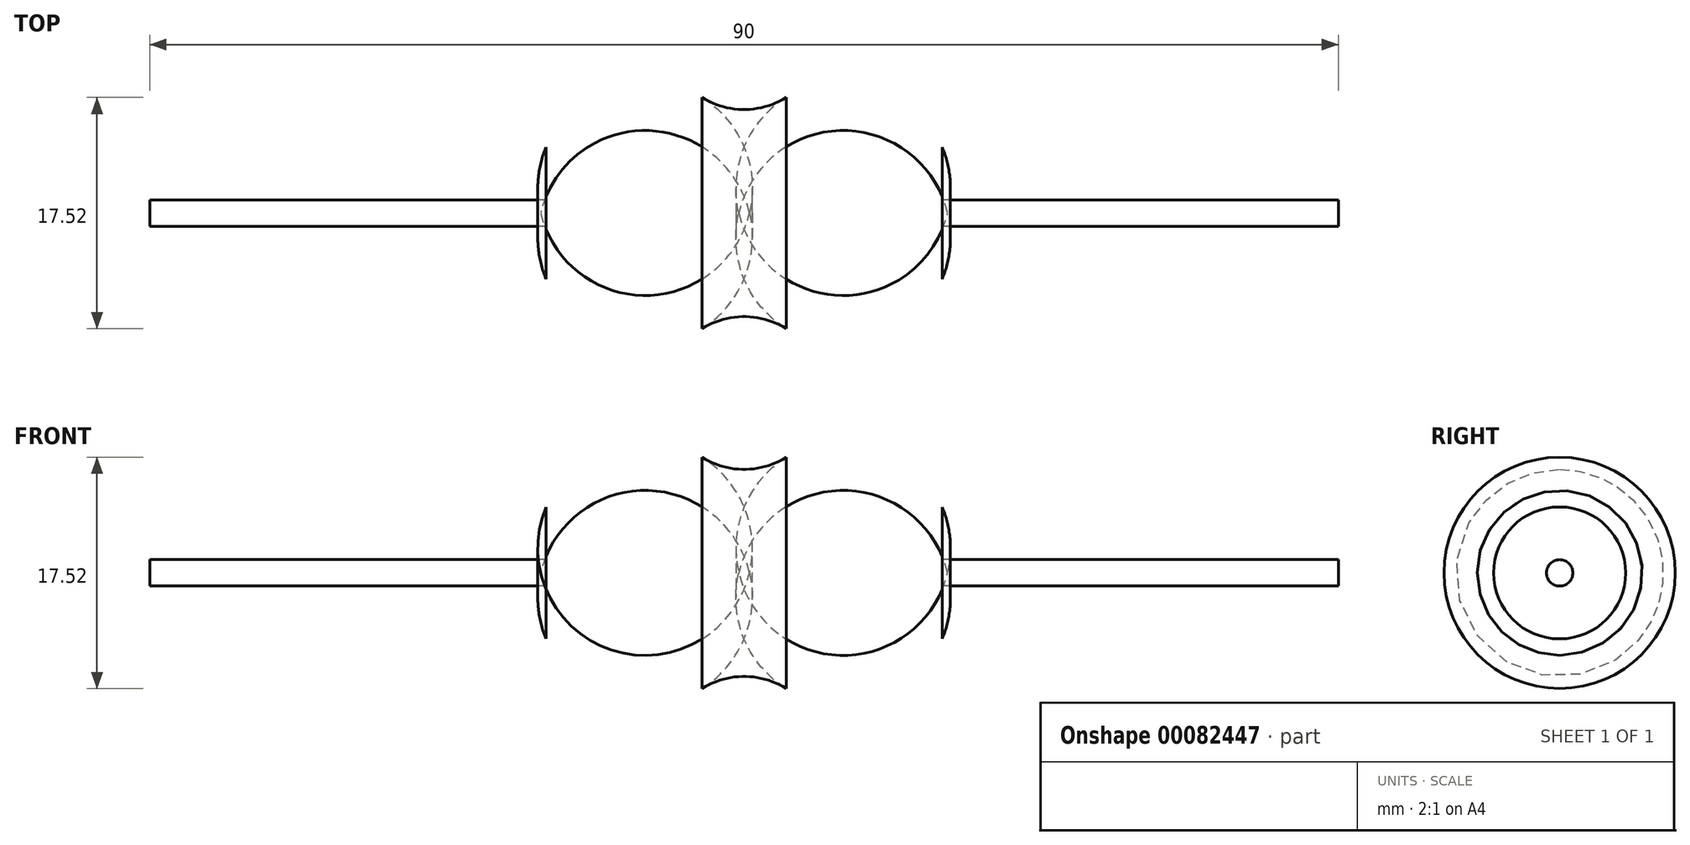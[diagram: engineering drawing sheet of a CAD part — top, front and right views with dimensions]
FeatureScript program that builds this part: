
annotation { "Feature Type Name" : "Feature", "Feature Type Description" : "" }
export const myFeature = defineFeature(function(context is Context, id is Id, definition is map)
    precondition{}
    {
        {
            var Q0;
            Q0=qCreatedBy(makeId("Front.planeOp"),FACE);
            var sketch = newSketch(context, id + "F0", { "sketchPlane" : qUnion([Q0])});
            skLineSegment(sketch, "E0.bottom", {"start": v(0, 0) * mm, "end": v(30, 0) * mm});
            skLineSegment(sketch, "E0.top", {"start": v(0, 10) * mm, "end": v(30, 10) * mm});
            skLineSegment(sketch, "E0.left", {"start": v(0, 0) * mm, "end": v(0, 10) * mm});
            skLineSegment(sketch, "E0.right", {"start": v(30, 0) * mm, "end": v(30, 10) * mm});
            skLineSegment(sketch, "E1", {"start": v(0, 5) * mm, "end": v(30, 5) * mm});
            skArc(sketch, "E2", {"start": v(11.81, 8.76) * mm, "mid": v(11.69, 8.84) * mm, "end": v(11.56, 8.91) * mm});
            skArc(sketch, "E3", {"start": v(30, 5) * mm, "mid": v(26.06, 9.18) * mm, "end": v(20.34, 9.7) * mm});
            skLineSegment(sketch, "E4.bottom", {"start": v(0, 0) * mm, "end": v(-30, 0) * mm});
            skLineSegment(sketch, "E4.top", {"start": v(0, 1) * mm, "end": v(-30, 1) * mm});
            skLineSegment(sketch, "E4.left", {"start": v(0, 0) * mm, "end": v(0, 1) * mm});
            skLineSegment(sketch, "E4.right", {"start": v(-30, 0) * mm, "end": v(-30, 1) * mm});
            skLineSegment(sketch, "E5.bottom", {"start": v(30, 0) * mm, "end": v(60, 0) * mm});
            skLineSegment(sketch, "E5.top", {"start": v(30, 1) * mm, "end": v(60, 1) * mm});
            skLineSegment(sketch, "E5.left", {"start": v(30, 0) * mm, "end": v(30, 1) * mm});
            skLineSegment(sketch, "E5.right", {"start": v(60, 0) * mm, "end": v(60, 1) * mm});
            skArc(sketch, "E6", {"start": v(9.3, 9.8) * mm, "mid": v(3.77, 9.1) * mm, "end": v(0, 5) * mm});
            skArc(sketch, "E7", {"start": v(11.56, 8.91) * mm, "mid": v(10.46, 9.44) * mm, "end": v(9.3, 9.8) * mm});
            skArc(sketch, "E8", {"start": v(18.46, 8.92) * mm, "mid": v(18.32, 8.84) * mm, "end": v(18.19, 8.76) * mm});
            skArc(sketch, "E9", {"start": v(20.34, 9.7) * mm, "mid": v(19.38, 9.38) * mm, "end": v(18.46, 8.92) * mm});
            skPoint(sketch, "E10.visualSharp", {"position": v(15, 5) * mm});
            skArc(sketch, "E10.filletArc", {"start": v(11.81, 8.76) * mm, "mid": v(15, 7.84) * mm, "end": v(18.19, 8.76) * mm});
            skSolve(sketch);
        }
        {
            var Q0;
            {var subQ7=sQuery(id+"F0.wireOp",EDGE,"E0.bottom");Q0=makeQuery(id+"F0.imprint","IMPRINT",FACE,{"disambiguationData":[TD([[makeQuery(id+"F0.imprint","IMPRINT",EDGE,{"derivedFrom":subQ7}),1.0]])]});}
            var Q1;
            {var subQ0=sQuery(id+"F0.wireOp",EDGE,"E2");var subQ4=makeQuery(id+"F0.imprint","INTERSECT",VERTEX,{"derivedFrom":[sQuery(id+"F0.wireOp",EDGE,"E0.top"),subQ0]});Q1=makeQuery(id+"F0.imprint","IMPRINT",FACE,{"disambiguationData":[TD([[makeQuery(id+"F0.imprint","IMPRINT",EDGE,{"disambiguationData":[TD([[subQ4,1.0]])],"derivedFrom":subQ0}),1.0]])]});}
            var Q2;
            {var subQ0=sQuery(id+"F0.wireOp",EDGE,"E3");var subQ4=makeQuery(id+"F0.imprint","INTERSECT",VERTEX,{"derivedFrom":[sQuery(id+"F0.wireOp",EDGE,"E0.top"),subQ0]});Q2=makeQuery(id+"F0.imprint","IMPRINT",FACE,{"disambiguationData":[TD([[makeQuery(id+"F0.imprint","IMPRINT",EDGE,{"disambiguationData":[TD([[subQ4,1.0]])],"derivedFrom":subQ0}),1.0]])]});}
            var Q3;
            Q3=sQuery(id+"F0.wireOp",EDGE,"E0.bottom");
            revolve(context, id + "F1", {"entities" : qUnion([Q0, Q1, Q2]), "axis" : qUnion([Q3]), "revolveType" : RevolveType.FULL});
        }
        {
            var Q0;
            Q0=makeQuery(id+"F0.imprint","IMPRINT",FACE,{"disambiguationData":[TD([[makeQuery(id+"F0.imprint","IMPRINT",EDGE,{"derivedFrom":sQuery(id+"F0.wireOp",EDGE,"E4.bottom")}),-1.0]])]});
            var Q1;
            Q1=makeQuery(id+"F0.imprint","IMPRINT",FACE,{"disambiguationData":[TD([[makeQuery(id+"F0.imprint","IMPRINT",EDGE,{"derivedFrom":sQuery(id+"F0.wireOp",EDGE,"E5.bottom")}),1.0]])]});
            var Q2;
            Q2=sQuery(id+"F0.wireOp",EDGE,"E5.bottom");
            var Q3;
            Q3=sQuery(id+"F0.wireOp",EDGE,"E5.right");
            var Q4;
            Q4=sQuery(id+"F0.wireOp",EDGE,"E5.top");
            var Q5;
            Q5=sQuery(id+"F0.wireOp",EDGE,"E0.right");
            var Q6;
            Q6=sQuery(id+"F0.wireOp",EDGE,"E0.bottom");
            revolve(context, id + "F2", {"entities" : qUnion([Q0, Q1]), "surfaceEntities" : qUnion([Q2, Q3, Q4, Q5]), "axis" : qUnion([Q6]), "revolveType" : RevolveType.FULL});
        }
        {
            var Q0;
            Q0=sQuery(id+"F0.wireOp",EDGE,"E7");
            var Q1;
            Q1=sQuery(id+"F0.wireOp",EDGE,"E9");
            var Q2;
            Q2=sQuery(id+"F0.wireOp",EDGE,"E0.bottom");
            revolve(context, id + "F3", {"bodyType" : ToolBodyType.SURFACE, "surfaceEntities" : qUnion([Q0, Q1]), "axis" : qUnion([Q2]), "revolveType" : RevolveType.FULL});
        }
    });
